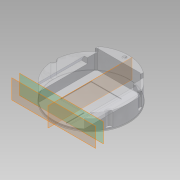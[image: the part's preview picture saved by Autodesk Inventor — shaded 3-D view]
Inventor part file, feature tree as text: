
AUTODESK INVENTOR PART (.ipt)
format: ipt  version: 2015 SP2 (Build 190223200, 223)  size: 270,848 bytes
history: native  units: mm
features: extrude x7, sketch x5, plane x3, chamfer x2, revolve x1, mirror x1, fillet x1, projected_geometry x1
ambient origin geometry x8: Origin, YZ Plane, XZ Plane, XY Plane, X Axis, Y Axis, Z Axis, Center Point
bodies: Solid1 (feature_tree)
feature tree (21):
  revolve  "Revolution1"  [1 undecoded]
  extrude  "Extrusion1"  Depth=25.5mm
  extrude  "Extrusion2"  Depth=4.363323mm
  extrude  "Extrusion3"  Depth=4.75mm TaperAngle=0.0deg
  extrude  "Extrusion5"  TaperAngle=0.0deg  [1 undecoded]
  plane  "Work Plane1"
  plane  "Work Plane3"
  plane  "Work Plane2"
  extrude  "Extrusion8"  Depth=0.25mm TaperAngle=0.0deg
  mirror  "Mirror1"
  chamfer  "Chamfer2"  Distance=21.5mm
  extrude  "Extrusion9"  Depth=0.25mm
  chamfer  "Chamfer3"  Distance=24.75mm
  extrude  "Extrusion10"  Depth=2.0mm
  fillet  "Fillet1"  Radius=1.0mm
  sketch  "Sketch2"  dims[d1=24.5mm d2=5.45mm]
  sketch  "Sketch7"  dims[d3=90.0deg d4=25.5mm]
  sketch  "Sketch10"  dims[d5=4.363323mm d6=4.363323mm]
  sketch  "Sketch11"  dims[d7=2.2mm d8=4.75mm d9=0.0mm]
  projected_geometry  "Projected Loop5"
  sketch  "Sketch12"  dims[d11=15.0mm d12=0.0mm d13=0.0mm d19=0.25mm d20=0.0mm d21=21.5mm d29=0.25mm d30=24.75mm d34=2.0mm d35=1.0mm d36=0.0mm d39=21.5mm d52=5.0mm d53=5.0mm d54=10.0mm d67=16.0mm d68=0.0mm d69=60.0deg d70=1.0mm d71=2.0mm d75=0.25mm d76=2.0mm d77=45.0deg d78=1.5mm d79=0.0mm d82=0.1mm d83=0.1mm d84=0.5mm d85=2.0mm d86=45.0deg d87=11.0mm d88=0.8mm d89=0.3mm d90=0.0mm d91=0.25mm d92=7.5mm d94=19.0mm d95=10.0mm d97=1.0mm d99=1.0mm d100=1.0mm d101=1.25mm]
note: 2 required parameter values undecoded (feature->parameter linkage not recoverable at this tier; creation-order binding heuristic only, values carry confidence <= 0.55)